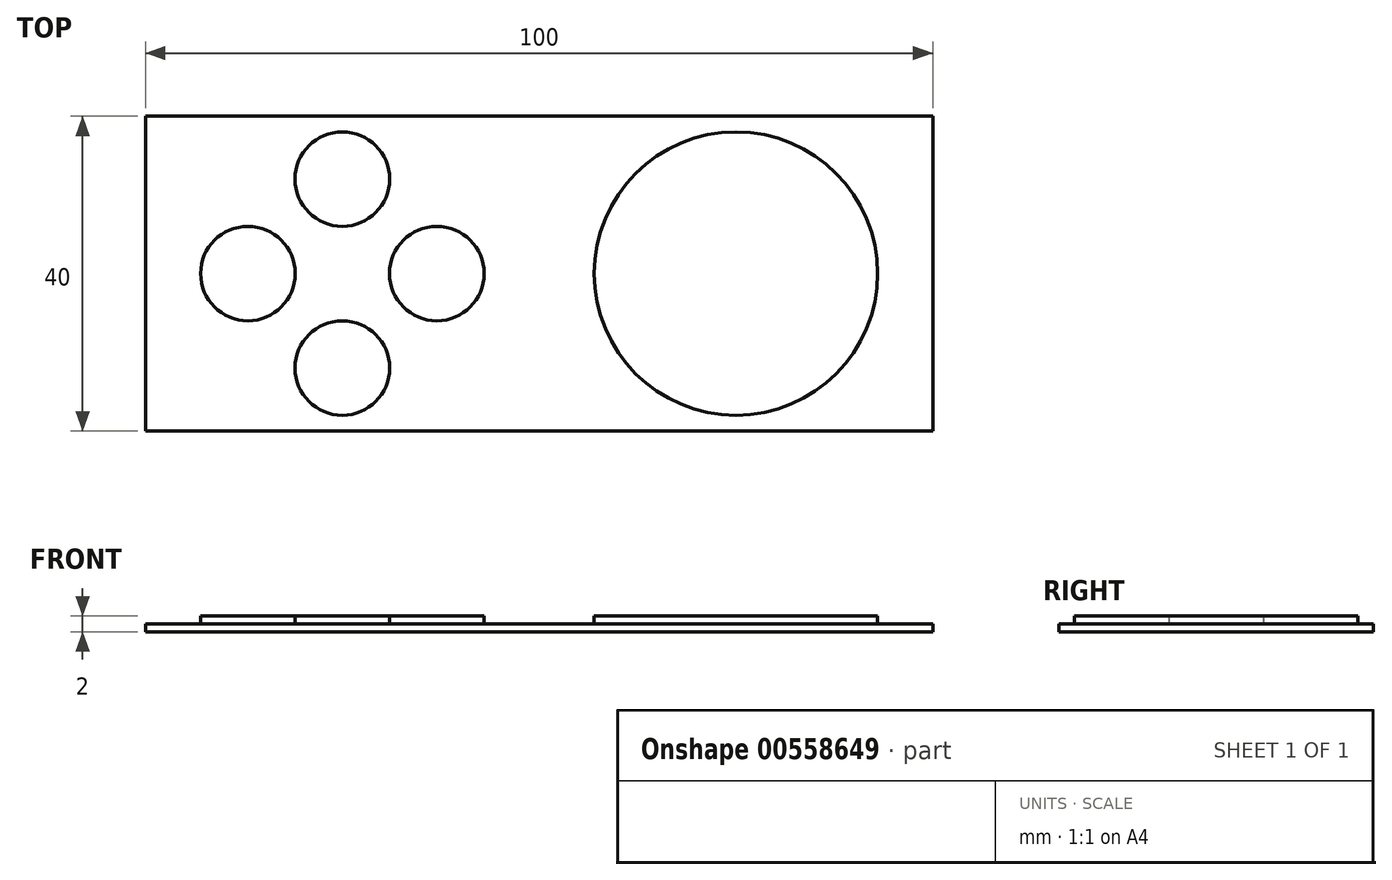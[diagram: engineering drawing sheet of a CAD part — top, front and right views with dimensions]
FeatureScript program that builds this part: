
annotation { "Feature Type Name" : "Feature", "Feature Type Description" : "" }
export const myFeature = defineFeature(function(context is Context, id is Id, definition is map)
    precondition{}
    {
        {
            var Q0;
            Q0=qCreatedBy(makeId("Top.planeOp"),FACE);
            var sketch = newSketch(context, id + "F0", { "sketchPlane" : qUnion([Q0])});
            skLineSegment(sketch, "E0.bottom", {"start": v(0, 0) * mm, "end": v(100, 0) * mm});
            skLineSegment(sketch, "E0.top", {"start": v(0, 40) * mm, "end": v(100, 40) * mm});
            skLineSegment(sketch, "E0.left", {"start": v(0, 0) * mm, "end": v(0, 40) * mm});
            skLineSegment(sketch, "E0.right", {"start": v(100, 0) * mm, "end": v(100, 40) * mm});
            skSolve(sketch);
        }
        {
            var Q0;
            Q0=makeQuery(id+"F0.imprint","IMPRINT",FACE,{"disambiguationData":[TD([[makeQuery(id+"F0.imprint","IMPRINT",EDGE,{"derivedFrom":sQuery(id+"F0.wireOp",EDGE,"E0.bottom")}),1.0]])]});
            extrude(context, id + "F1", {"entities" : qUnion([Q0]), "depth" : 1 * mm, "offsetDistance" : 25 * mm});
        }
        {
            var Q0;
            Q0=makeQuery(id+"F1.opExtrude","CAP_FACE",FACE,{"disambiguationData":[OSD([sQuery(id+"F0.wireOp",EDGE,"E0.bottom"),sQuery(id+"F0.wireOp",EDGE,"E0.top"),sQuery(id+"F0.wireOp",EDGE,"E0.left"),sQuery(id+"F0.wireOp",EDGE,"E0.right")])],"isStart":false});
            var sketch = newSketch(context, id + "F2", { "sketchPlane" : qUnion([Q0])});
            skLineSegment(sketch, "E1", {"start": v(50, 40) * mm, "end": v(50, 0) * mm, "construction": true});
            skLineSegment(sketch, "E2", {"start": v(0, 20) * mm, "end": v(100, 20) * mm, "construction": true});
            skLineSegment(sketch, "E3", {"start": v(0, 24.78) * mm, "end": v(50, 24.78) * mm, "construction": true});
            skLineSegment(sketch, "E4", {"start": v(25, 24.78) * mm, "end": v(25, 0) * mm, "construction": true});
            skLineSegment(sketch, "E5", {"start": v(25, 0) * mm, "end": v(25, 40) * mm, "construction": true});
            skLineSegment(sketch, "E6", {"start": v(50, 14.03) * mm, "end": v(100, 14.03) * mm, "construction": true});
            skLineSegment(sketch, "E7", {"start": v(75, 14.03) * mm, "end": v(75, 0) * mm, "construction": true});
            skLineSegment(sketch, "E8", {"start": v(75, 0) * mm, "end": v(75, 40) * mm, "construction": true});
            skCircle(sketch, "E9", {"center": v(13, 20) * mm, "radius": 6 * mm});
            skCircle(sketch, "E10", {"center": v(25, 32) * mm, "radius": 6 * mm});
            skCircle(sketch, "E11", {"center": v(37, 20) * mm, "radius": 6 * mm});
            skCircle(sketch, "E12", {"center": v(75, 20) * mm, "radius": 18 * mm});
            skCircle(sketch, "E13", {"center": v(25, 8) * mm, "radius": 6 * mm});
            skSolve(sketch);
        }
        {
            var Q0;
            Q0 = qSketchRegion(id + "F2", true);
            extrude(context, id + "F3", {"entities" : qUnion([Q0]), "operationType" : NewBodyOperationType.ADD, "depth" : 1 * mm, "offsetDistance" : 25 * mm});
        }
    });
